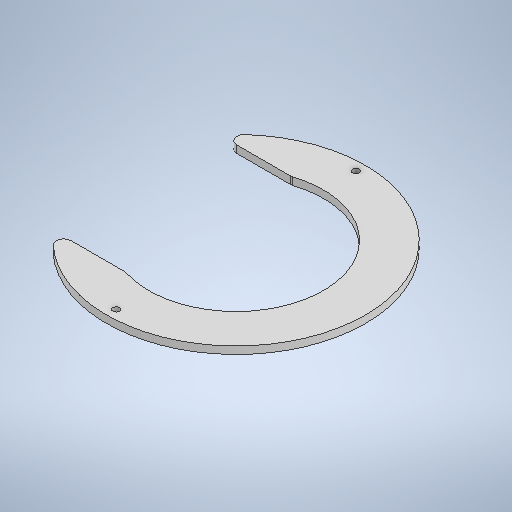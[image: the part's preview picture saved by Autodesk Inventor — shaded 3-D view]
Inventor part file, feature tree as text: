
AUTODESK INVENTOR PART (.ipt)
format: ipt  version: 2025.2 (Build 292293000, 293)  size: 270,848 bytes
history: native  units: in
note: dims shown in document units (in); Inventor stores cm internally (conversion verified against a paired STEP export)
features: extrude x1, fillet x1, sketch x1
ambient origin geometry x8: Origin, YZ Plane, XZ Plane, XY Plane, X Axis, Y Axis, Z Axis, Center Point
bodies: Solid1 (feature_tree)
feature tree (3):
  extrude  "Extrusion1"  Depth=0.1969in
  fillet  "Fillet1"  Radius=6.8898in
  sketch  "Sketch1"  dims[d0=4.6457in d1=6.378in d2=6.8898in d3=0.1772in d4=0.1772in d5=0.1969in d6=0.0in d7=4.4094in d9=3.1496in d10=0.3937in d11=0.1969in d12=0.1969in]
